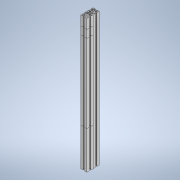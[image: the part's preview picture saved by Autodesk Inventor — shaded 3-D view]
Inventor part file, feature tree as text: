
AUTODESK INVENTOR PART (.ipt)
format: ipt  version: 2022 (Build 260153000, 153)  size: 455,680 bytes
history: native  units: in
note: dims shown in document units (in); Inventor stores cm internally (conversion verified against a paired STEP export)
features: sketch x12, extrude x6, hole x5, plane x3
ambient origin geometry x8: Origin, YZ Plane, XZ Plane, XY Plane, X Axis, Y Axis, Z Axis, Center Point
bodies: Solid4 (feature_tree), Solid5 (feature_tree), Solid6 (feature_tree), Solid7 (feature_tree), Solid8 (feature_tree)
feature tree (26):
  plane  "Work Plane1"
  extrude  "Extrusion1"  Depth=16.9685in TaperAngle=0.0deg
  hole  "Hole1"  [1 undecoded]
  plane  "Work Plane2"
  extrude  "Extrusion2"  Depth=14.7638in
  hole  "Hole3"  [1 undecoded]
  plane  "Work Plane3"
  extrude  "Extrusion3"  Depth=16.9685in TaperAngle=0.0deg
  hole  "Hole4"  [1 undecoded]
  extrude  "Extrusion4"  [1 undecoded]
  extrude  "Extrusion5"  [1 undecoded]
  hole  "Hole6"  [1 undecoded]
  extrude  "Extrusion6"  [1 undecoded]
  hole  "Hole7"  [1 undecoded]
  sketch  "Sketch1"  dims[d0=16.9685in d1=16.9685in d2=0.0in]
  sketch  "Sketch2"  dims[d3=0.1575in d4=0.2362in d5=0.1575in d6=0.0787in d7=90.0deg d8=0.315in d9=0.8108in]
  sketch  "Sketch3"  dims[d10=0.1575in d11=0.2362in d12=0.1575in d13=0.0787in d14=90.0deg d15=0.315in d16=0.8108in d17=4.8031in]
  sketch  "Sketch4"  dims[d18=4.8031in d19=0.0in]
  sketch  "Sketch5"  dims[d20=0.1575in d21=0.2362in d22=0.1575in d23=0.0787in d24=90.0deg d25=0.315in d26=0.8108in d27=14.7638in]
  sketch  "Sketch6"  dims[d28=14.7638in d29=0.0in]
  sketch  "Sketch7"  dims[d30=0.1575in d31=0.2362in d32=0.1575in d33=0.0787in d34=90.0deg d35=0.315in d36=0.8108in d37=15.748in d38=0.0in]
  sketch  "Sketch8"  dims[d39=14.7638in d40=0.0in]
  sketch  "Sketch9"  dims[d41=0.1575in d42=0.2362in d43=0.1575in d44=0.0787in d45=90.0deg d46=0.315in d47=0.8108in d48=16.9685in d49=0.0in]
  sketch  "Sketch10"  dims[d50=0.1575in d51=0.2362in d52=0.1575in d53=0.0787in d54=90.0deg d55=0.315in d56=0.8108in]
  sketch  "Sketch11"
  sketch  "Sketch12"
note: 8 required parameter values undecoded (feature->parameter linkage not recoverable at this tier; creation-order binding heuristic only, values carry confidence <= 0.55)
